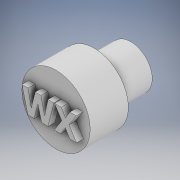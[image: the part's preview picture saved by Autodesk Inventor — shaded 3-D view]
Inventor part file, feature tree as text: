
AUTODESK INVENTOR PART (.ipt)
format: ipt  version: 2022 (Build 260153000, 153)  size: 153,088 bytes
history: native  units: in
note: dims shown in document units (in); Inventor stores cm internally (conversion verified against a paired STEP export)
features: extrude x3, sketch x2
ambient origin geometry x8: Origin, YZ Plane, XZ Plane, XY Plane, X Axis, Y Axis, Z Axis, Center Point
bodies: Body1 (feature_tree)
feature tree (5):
  sketch  "Sketch1"  dims[d16=0.389in d17=0.0185in]
  extrude  "Extrusion8"  Depth=0.0185in
  extrude  "Extrusion9"  Depth=0.189in TaperAngle=0.0deg
  extrude  "Extrusion10"  Depth=0.0354in TaperAngle=0.0deg
  sketch  "Sketch4"  dims[d18=0.1969in d19=0.0in d20=0.189in d21=0.0in d22=0.0354in d23=0.0in]
